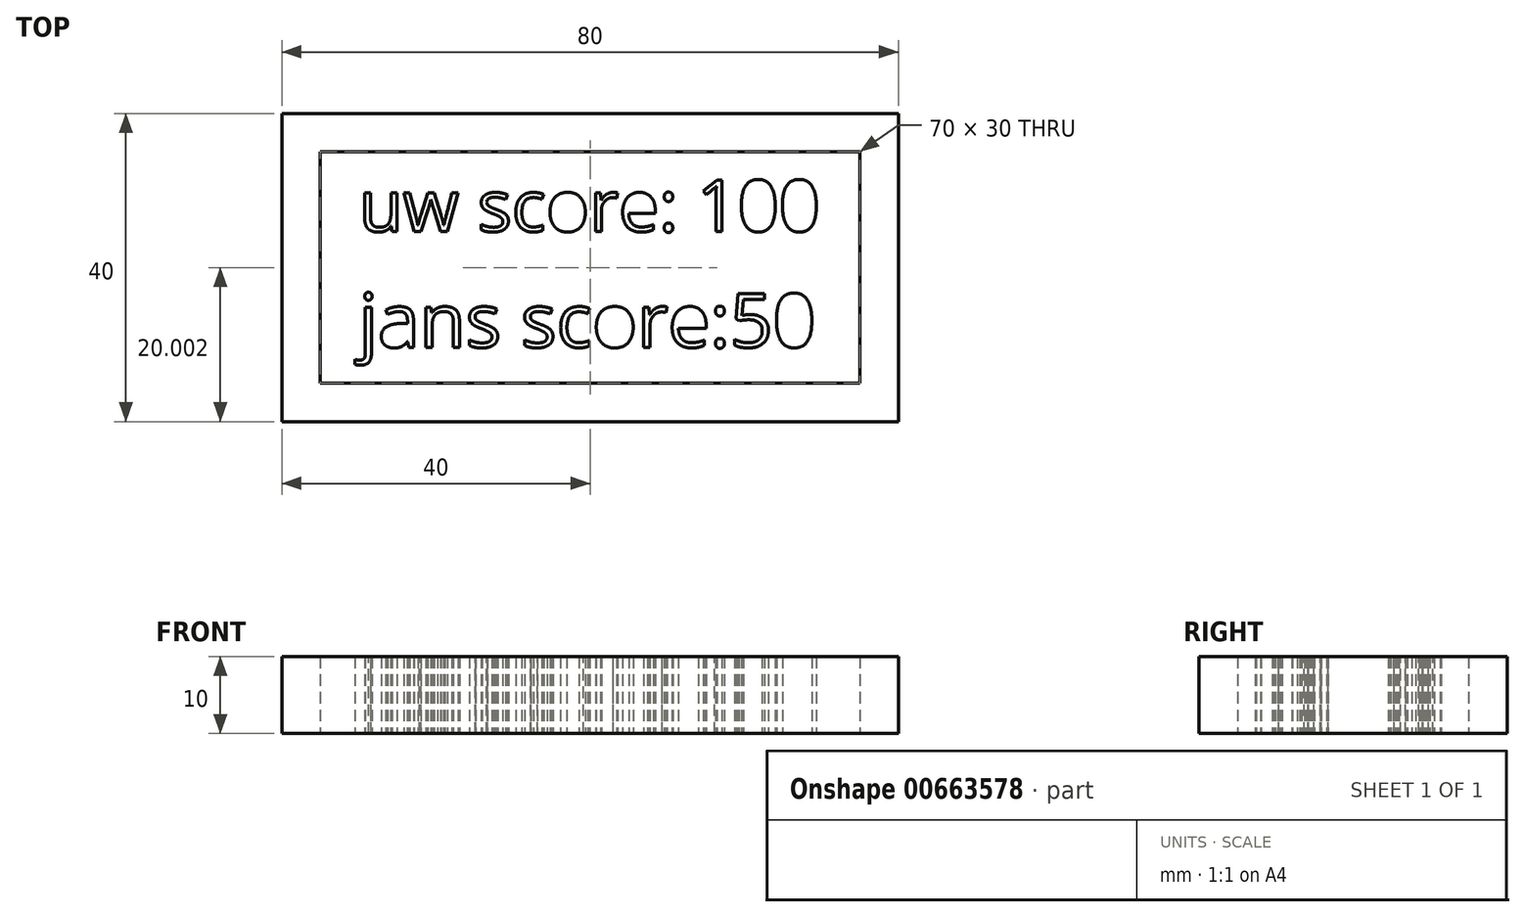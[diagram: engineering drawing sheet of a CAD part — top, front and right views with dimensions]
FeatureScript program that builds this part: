
annotation { "Feature Type Name" : "Feature", "Feature Type Description" : "" }
export const myFeature = defineFeature(function(context is Context, id is Id, definition is map)
    precondition{}
    {
        {
            var Q0;
            Q0=qCreatedBy(makeId("Top.planeOp"),FACE);
            var sketch = newSketch(context, id + "F0", { "sketchPlane" : qUnion([Q0])});
            skLineSegment(sketch, "E0.bottom", {"start": v(-75, -0.78) * mm, "end": v(5, -0.78) * mm});
            skLineSegment(sketch, "E0.top", {"start": v(-75, -40.78) * mm, "end": v(5, -40.78) * mm});
            skLineSegment(sketch, "E0.left", {"start": v(-75, -0.78) * mm, "end": v(-75, -40.78) * mm});
            skLineSegment(sketch, "E0.right", {"start": v(5, -0.78) * mm, "end": v(5, -40.78) * mm});
            skLineSegment(sketch, "E1.bottom", {"start": v(-70, -5.78) * mm, "end": v(0, -5.78) * mm});
            skLineSegment(sketch, "E1.top", {"start": v(-70, -35.78) * mm, "end": v(0, -35.78) * mm});
            skLineSegment(sketch, "E1.left", {"start": v(-70, -5.78) * mm, "end": v(-70, -35.78) * mm});
            skLineSegment(sketch, "E1.right", {"start": v(0, -5.78) * mm, "end": v(0, -35.78) * mm});
            skLineSegment(sketch, "E2", {"start": v(-70, -20.78) * mm, "end": v(0, -20.78) * mm});
            skText(sketch, "E3", { "text": "uw score: 100", "fontName": "OpenSans-Regular.ttf"});
            skText(sketch, "E4", { "text": "jans score:50", "fontName": "OpenSans-Regular.ttf"});
            const initialGuessF0  = {"E3": [-0.065, -0.0161, 1, 0, 0.00671], "E4": [-0.065, -0.03113, 1, 0, 0.007]};
            skSetInitialGuess(sketch, initialGuessF0);
            skSolve(sketch);
        }
        {
            var Q0;
            Q0 = qSketchRegion(id + "F0", true);
            var Q1;
            Q1=makeQuery(id+"F0.imprint","IMPRINT",FACE,{"disambiguationData":[TD([[makeQuery(id+"F0.imprint","IMPRINT",EDGE,{"derivedFrom":sQuery(id+"F0.wireOp",EDGE,"E4.sketch_text.stroke-135")}),1.0]])]});
            var Q2;
            Q2=makeQuery(id+"F0.imprint","IMPRINT",FACE,{"disambiguationData":[TD([[makeQuery(id+"F0.imprint","IMPRINT",EDGE,{"derivedFrom":sQuery(id+"F0.wireOp",EDGE,"E0.bottom")}),-1.0]])]});
            var Q3;
            Q3=makeQuery(id+"F0.imprint","IMPRINT",FACE,{"disambiguationData":[TD([[makeQuery(id+"F0.imprint","IMPRINT",EDGE,{"derivedFrom":sQuery(id+"F0.wireOp",EDGE,"E3.sketch_text.stroke-89")}),1.0]])]});
            var Q4;
            Q4=makeQuery(id+"F0.imprint","IMPRINT",FACE,{"disambiguationData":[TD([[makeQuery(id+"F0.imprint","IMPRINT",EDGE,{"derivedFrom":sQuery(id+"F0.wireOp",EDGE,"E3.sketch_text.stroke-160")}),1.0]])]});
            var Q5;
            Q5=makeQuery(id+"F0.imprint","IMPRINT",FACE,{"disambiguationData":[TD([[makeQuery(id+"F0.imprint","IMPRINT",EDGE,{"derivedFrom":sQuery(id+"F0.wireOp",EDGE,"E3.sketch_text.stroke-176")}),1.0]])]});
            var Q6;
            Q6=makeQuery(id+"F0.imprint","IMPRINT",FACE,{"disambiguationData":[TD([[makeQuery(id+"F0.imprint","IMPRINT",EDGE,{"derivedFrom":sQuery(id+"F0.wireOp",EDGE,"E4.sketch_text.stroke-216")}),1.0]])]});
            var Q7;
            Q7=makeQuery(id+"F0.imprint","IMPRINT",FACE,{"disambiguationData":[TD([[makeQuery(id+"F0.imprint","IMPRINT",EDGE,{"derivedFrom":sQuery(id+"F0.wireOp",EDGE,"E4.sketch_text.stroke-208")}),-1.0]])]});
            var Q8;
            Q8=makeQuery(id+"F0.imprint","IMPRINT",FACE,{"disambiguationData":[TD([[makeQuery(id+"F0.imprint","IMPRINT",EDGE,{"derivedFrom":sQuery(id+"F0.wireOp",EDGE,"E4.sketch_text.stroke-86")}),-1.0]])]});
            var Q9;
            Q9=makeQuery(id+"F0.imprint","IMPRINT",FACE,{"disambiguationData":[TD([[makeQuery(id+"F0.imprint","IMPRINT",EDGE,{"derivedFrom":sQuery(id+"F0.wireOp",EDGE,"E4.sketch_text.stroke-156")}),-1.0]])]});
            var Q10;
            Q10=makeQuery(id+"F0.imprint","IMPRINT",FACE,{"disambiguationData":[TD([[makeQuery(id+"F0.imprint","IMPRINT",EDGE,{"derivedFrom":sQuery(id+"F0.wireOp",EDGE,"E4.sketch_text.stroke-143")}),-1.0]])]});
            var Q11;
            Q11=makeQuery(id+"F0.imprint","IMPRINT",FACE,{"disambiguationData":[TD([[makeQuery(id+"F0.imprint","IMPRINT",EDGE,{"derivedFrom":sQuery(id+"F0.wireOp",EDGE,"E4.sketch_text.stroke-111")}),-1.0]])]});
            var Q12;
            Q12=makeQuery(id+"F0.imprint","IMPRINT",FACE,{"disambiguationData":[TD([[makeQuery(id+"F0.imprint","IMPRINT",EDGE,{"derivedFrom":sQuery(id+"F0.wireOp",EDGE,"E4.sketch_text.stroke-126")}),-1.0]])]});
            var Q13;
            Q13=makeQuery(id+"F0.imprint","IMPRINT",FACE,{"disambiguationData":[TD([[makeQuery(id+"F0.imprint","IMPRINT",EDGE,{"derivedFrom":sQuery(id+"F0.wireOp",EDGE,"E4.sketch_text.stroke-61")}),-1.0]])]});
            var Q14;
            Q14=makeQuery(id+"F0.imprint","IMPRINT",FACE,{"disambiguationData":[TD([[makeQuery(id+"F0.imprint","IMPRINT",EDGE,{"derivedFrom":sQuery(id+"F0.wireOp",EDGE,"E3.sketch_text.stroke-168")}),-1.0]])]});
            var Q15;
            Q15=makeQuery(id+"F0.imprint","IMPRINT",FACE,{"disambiguationData":[TD([[makeQuery(id+"F0.imprint","IMPRINT",EDGE,{"derivedFrom":sQuery(id+"F0.wireOp",EDGE,"E3.sketch_text.stroke-152")}),-1.0]])]});
            var Q16;
            Q16=makeQuery(id+"F0.imprint","IMPRINT",FACE,{"disambiguationData":[TD([[makeQuery(id+"F0.imprint","IMPRINT",EDGE,{"derivedFrom":sQuery(id+"F0.wireOp",EDGE,"E4.sketch_text.stroke-17")}),-1.0]])]});
            var Q17;
            Q17=makeQuery(id+"F0.imprint","IMPRINT",FACE,{"disambiguationData":[TD([[makeQuery(id+"F0.imprint","IMPRINT",EDGE,{"derivedFrom":sQuery(id+"F0.wireOp",EDGE,"E3.sketch_text.stroke-110")}),-1.0]])]});
            var Q18;
            Q18=makeQuery(id+"F0.imprint","IMPRINT",FACE,{"disambiguationData":[TD([[makeQuery(id+"F0.imprint","IMPRINT",EDGE,{"derivedFrom":sQuery(id+"F0.wireOp",EDGE,"E3.sketch_text.stroke-80")}),-1.0]])]});
            var Q19;
            Q19=makeQuery(id+"F0.imprint","IMPRINT",FACE,{"disambiguationData":[TD([[makeQuery(id+"F0.imprint","IMPRINT",EDGE,{"derivedFrom":sQuery(id+"F0.wireOp",EDGE,"E4.sketch_text.stroke-175")}),-1.0]])]});
            var Q20;
            Q20=makeQuery(id+"F0.imprint","IMPRINT",FACE,{"disambiguationData":[TD([[makeQuery(id+"F0.imprint","IMPRINT",EDGE,{"derivedFrom":sQuery(id+"F0.wireOp",EDGE,"E4.sketch_text.stroke-44")}),-1.0]])]});
            var Q21;
            Q21=makeQuery(id+"F0.imprint","IMPRINT",FACE,{"disambiguationData":[TD([[makeQuery(id+"F0.imprint","IMPRINT",EDGE,{"derivedFrom":sQuery(id+"F0.wireOp",EDGE,"E4.sketch_text.stroke-36")}),1.0]])]});
            var Q22;
            Q22=makeQuery(id+"F0.imprint","IMPRINT",FACE,{"disambiguationData":[TD([[makeQuery(id+"F0.imprint","IMPRINT",EDGE,{"derivedFrom":sQuery(id+"F0.wireOp",EDGE,"E3.sketch_text.stroke-0")}),-1.0]])]});
            var Q23;
            Q23=makeQuery(id+"F0.imprint","IMPRINT",FACE,{"disambiguationData":[TD([[makeQuery(id+"F0.imprint","IMPRINT",EDGE,{"derivedFrom":sQuery(id+"F0.wireOp",EDGE,"E3.sketch_text.stroke-17")}),-1.0]])]});
            var Q24;
            Q24=makeQuery(id+"F0.imprint","IMPRINT",FACE,{"disambiguationData":[TD([[makeQuery(id+"F0.imprint","IMPRINT",EDGE,{"derivedFrom":sQuery(id+"F0.wireOp",EDGE,"E3.sketch_text.stroke-40")}),-1.0]])]});
            var Q25;
            Q25=makeQuery(id+"F0.imprint","IMPRINT",FACE,{"disambiguationData":[TD([[makeQuery(id+"F0.imprint","IMPRINT",EDGE,{"derivedFrom":sQuery(id+"F0.wireOp",EDGE,"E3.sketch_text.stroke-65")}),-1.0]])]});
            var Q26;
            Q26=makeQuery(id+"F0.imprint","IMPRINT",FACE,{"disambiguationData":[TD([[makeQuery(id+"F0.imprint","IMPRINT",EDGE,{"derivedFrom":sQuery(id+"F0.wireOp",EDGE,"E3.sketch_text.stroke-97")}),-1.0]])]});
            var Q27;
            Q27=makeQuery(id+"F0.imprint","IMPRINT",FACE,{"disambiguationData":[TD([[makeQuery(id+"F0.imprint","IMPRINT",EDGE,{"derivedFrom":sQuery(id+"F0.wireOp",EDGE,"E3.sketch_text.stroke-129")}),-1.0]])]});
            var Q28;
            Q28=makeQuery(id+"F0.imprint","IMPRINT",FACE,{"disambiguationData":[TD([[makeQuery(id+"F0.imprint","IMPRINT",EDGE,{"derivedFrom":sQuery(id+"F0.wireOp",EDGE,"E3.sketch_text.stroke-137")}),-1.0]])]});
            var Q29;
            Q29=makeQuery(id+"F0.imprint","IMPRINT",FACE,{"disambiguationData":[TD([[makeQuery(id+"F0.imprint","IMPRINT",EDGE,{"derivedFrom":sQuery(id+"F0.wireOp",EDGE,"E3.sketch_text.stroke-143")}),-1.0]])]});
            var Q30;
            Q30=makeQuery(id+"F0.imprint","IMPRINT",FACE,{"disambiguationData":[TD([[makeQuery(id+"F0.imprint","IMPRINT",EDGE,{"derivedFrom":sQuery(id+"F0.wireOp",EDGE,"E4.sketch_text.stroke-0")}),-1.0]])]});
            var Q31;
            Q31=makeQuery(id+"F0.imprint","IMPRINT",FACE,{"disambiguationData":[TD([[makeQuery(id+"F0.imprint","IMPRINT",EDGE,{"derivedFrom":sQuery(id+"F0.wireOp",EDGE,"E4.sketch_text.stroke-183")}),-1.0]])]});
            var Q32;
            Q32=makeQuery(id+"F0.imprint","IMPRINT",FACE,{"disambiguationData":[TD([[makeQuery(id+"F0.imprint","IMPRINT",EDGE,{"derivedFrom":sQuery(id+"F0.wireOp",EDGE,"E4.sketch_text.stroke-189")}),-1.0]])]});
            var Q33;
            Q33=makeQuery(id+"F0.imprint","IMPRINT",FACE,{"disambiguationData":[TD([[makeQuery(id+"F0.imprint","IMPRINT",EDGE,{"derivedFrom":sQuery(id+"F0.wireOp",EDGE,"E4.sketch_text.stroke-170")}),1.0]])]});
            var Q34;
            Q34=makeQuery(id+"F0.imprint","IMPRINT",FACE,{"disambiguationData":[TD([[makeQuery(id+"F0.imprint","IMPRINT",EDGE,{"derivedFrom":sQuery(id+"F0.wireOp",EDGE,"E4.sketch_text.stroke-9")}),-1.0]])]});
            var Q35;
            Q35=makeQuery(id+"F0.imprint","IMPRINT",FACE,{"disambiguationData":[TD([[makeQuery(id+"F0.imprint","IMPRINT",EDGE,{"derivedFrom":sQuery(id+"F0.wireOp",EDGE,"E3.sketch_text.stroke-124")}),1.0]])]});
            extrude(context, id + "F1", {"entities" : qUnion([Q0, Q1, Q2, Q3, Q4, Q5, Q6, Q7, Q8, Q9, Q10, Q11, Q12, Q13, Q14, Q15, Q16, Q17, Q18, Q19, Q20, Q21, Q22, Q23, Q24, Q25, Q26, Q27, Q28, Q29, Q30, Q31, Q32, Q33, Q34, Q35]), "depth" : 10 * mm, "offsetDistance" : 25 * mm});
        }
    });
